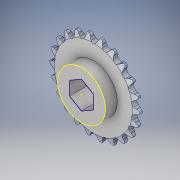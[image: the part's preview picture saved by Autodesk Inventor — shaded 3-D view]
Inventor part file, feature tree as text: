
AUTODESK INVENTOR PART (.ipt)
format: ipt  version: 2017 (Build 210142000, 142)  size: 627,712 bytes
history: native  units: in
note: dims shown in document units (in); Inventor stores cm internally (conversion verified against a paired STEP export)
features: sketch x1, projected_geometry x1, other x1
ambient origin geometry x8: Origin, YZ Plane, XZ Plane, XY Plane, X Axis, Y Axis, Z Axis, Center Point
bodies: Solid1 (feature_tree)
feature tree (3):
  sketch  "Sketch1"
  projected_geometry  "Projected Loop1"
  other  "Cut-Extrude2"
